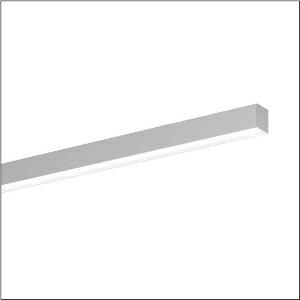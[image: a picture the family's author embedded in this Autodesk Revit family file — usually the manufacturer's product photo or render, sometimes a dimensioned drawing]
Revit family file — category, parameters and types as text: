
# Revit family: silica_r__21_51mx20tbt2s_686e
name_source: partatom
category: Lighting Fixtures
units: mm (PartAtom-declared; Revit-internal decimal feet)

## family parameters
Cut with Voids When Loaded = No
Host = Face
Light Source = No
Part Type = Normal
Room Calculation Point = No
Round Connector Dimension = Use Diameter
Shared = No

## types (1)
- --- (1 x LED, 3000 lm, 25.6 W, 6500K)
    Apparent Load = 26 VA
    CIE Flux Codes = 48 79 96 100 100
    Color Rendering = 80
    Color Temperature = 6500K
    Default Elevation = 1800 mm
    Description = Silica® 21, office luminaire, primary optical cover: cover, of PMMA, opal, light emission: direct distribution, primary light characteristic: symmetric, installation type: surface-mounted, LED, rated luminous flux: 3.000lm, luminous efficacy: 112lm/W, light colour: 8tw, colour temperature: 2700..6500K, control gear: ECG DALI, with terminal, 3+2-pole, max. 2.5mm², mains connection: 220..240V, AC, 50/60Hz, rated input power: 26.9W, luminaire housing, of aluminium, metallic grey (RAL 9006), length: 1.504mm, width: 53mm, height: 53mm, protection rating (complete): IP20, insulation class (complete): insulation class I (protective earthing), certification: CE, permissible operating ambient temperature: 0..+35°C, standard: EN 50419, packaging unit: 1 piece
    Height = 0 mm  [stored 0 ft]
    Lamp = 1 x LED
    Lamp Light Flux = 3000 lm
    Lamp Power = 25.6 W
    Lamp count = 1
    Length = 1504 mm
    Luminous efficacy = 117 lm/W
    Manufacturer = Siteco
    ModVariant = No
    Model = 51MX20TBT2S
    Mounting Place = Ceiling
    Mounting Type = Recessed
    Number of Poles = 1
    OnlyDefault = Yes
    Power Factor = 1
    Product Name = Silica® 21
    Product group = office luminaire | ceiling recessed
    ProductGroupID = 400
    Protection Class = Protection class I
    Protection Degree = IP 20
    RLX_Detail_Level = 1
    RLX_Emergency_Light_Flux = 0 lm
    RLX_Emergency_Type = 0
    RLX_Emergency_Type_DB = No
    RlxData = <blob elided: 23217 chars, md5=416a99a0>
    Socket = socket
    Standby Power = 0 W
    System Light Flux = 3000 lm
    System Power = 26 W
    Type Comments = individual setting
    Type Image = l_1335933.jpg
    URL = http://relux.com
    VarID = @adj_109471
    Voltage = 0 V
    Weight = 0.00 kg
    Width = 53 mm

note: [stored X ft] marks values corroborated as IEEE doubles in the binary element streams (Revit-internal decimal feet)

## geometry (parser evidence)
native form markers: Blend x4, Sweep x10
no freeform markers — native parametric forms only
